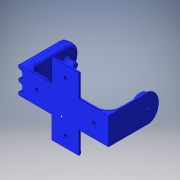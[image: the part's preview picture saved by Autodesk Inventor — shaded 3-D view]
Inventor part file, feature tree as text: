
AUTODESK INVENTOR PART (.ipt)
format: ipt  version: 2016 (Build 200138000, 138)  size: 598,016 bytes
history: native  units: in
note: dims shown in document units (in); Inventor stores cm internally (conversion verified against a paired STEP export)
features: extrude x12, sketch x12, fillet x11, hole x2
ambient origin geometry x8: Origin, YZ Plane, XZ Plane, XY Plane, X Axis, Y Axis, Z Axis, Center Point
bodies: Solid1 (feature_tree)
feature tree (37):
  extrude  "Extrusion1"  Depth=0.5197in
  extrude  "Extrusion3"  Depth=0.0787in
  sketch  "Sketch5"  dims[d9=0.9449in d10=0.0in d11=0.2835in]
  extrude  "Extrusion4"  Depth=0.2835in
  extrude  "Extrusion5"  Depth=0.2598in
  fillet  "Fillet1"  Radius=0.2598in
  fillet  "Fillet4"  Radius=0.5197in
  fillet  "Fillet5"  Radius=0.3622in
  fillet  "Fillet6"  Radius=0.1437in
  fillet  "Fillet7"  Radius=0.2224in
  extrude  "Extrusion6"  Depth=0.0787in
  sketch  "Sketch9"  dims[d24=0.0787in d25=0.0in d27=0.0787in]
  extrude  "Extrusion7"  Depth=0.1969in
  fillet  "Fillet10"  Radius=0.0197in
  fillet  "Fillet11"  Radius=0.0394in
  sketch  "Sketch10"  dims[d28=0.0787in d29=0.0in d30=0.1969in d33=0.0197in d34=0.0394in]
  extrude  "Extrusion8"  Depth=0.0197in
  extrude  "Extrusion10"  Depth=0.9449in TaperAngle=0.0deg
  extrude  "Extrusion11"  Depth=0.2598in
  sketch  "Sketch17"  dims[d43=0.2598in d44=0.2598in]
  hole  "Hole2"  [1 undecoded]
  fillet  "Fillet18"  Radius=0.1772in
  extrude  "Extrusion12"  Depth=0.0197in
  extrude  "Extrusion13"  Depth=0.0276in TaperAngle=0.0deg
  fillet  "Fillet22"  Radius=0.5197in
  hole  "Hole3"  [1 undecoded]
  extrude  "Extrusion14"  Depth=0.0276in
  fillet  "Fillet24"  Radius=0.4291in
  fillet  "Fillet25"  Radius=0.5669in
  sketch  "Sketch1"  dims[d0=1.6535in d1=0.5197in]
  sketch  "Sketch4"  dims[d2=0.0787in d3=0.0in d8=0.0787in]
  sketch  "Sketch7"  dims[d12=0.2598in d13=0.2598in d14=0.2598in d15=0.5197in d16=0.3622in d17=0.1437in d19=0.2224in]
  sketch  "Sketch15"  dims[d35=0.0394in d36=0.0197in]
  sketch  "Sketch16"  dims[d37=0.0787in d38=0.9449in d39=0.0in]
  sketch  "Sketch18"  dims[d45=0.2598in d46=0.1181in d47=0.1772in d48=0.0in]
  sketch  "Sketch19"  dims[d49=0.0394in d50=0.0197in]
  sketch  "Sketch20"  dims[d51=0.1181in d52=0.1181in d53=0.0in d82=0.5197in d83=0.5669in d84=0.5669in d85=0.4291in d86=0.0in d87=0.5669in d88=0.4291in d89=0.0in d90=0.0591in d91=0.2362in d92=0.1575in d93=0.0787in d94=90.0deg d95=0.315in d96=0.8108in d98=0.1181in d99=0.5591in d100=0.5591in d101=0.5591in d103=0.4291in d104=0.0in d106=0.0591in d107=0.4291in d108=0.0in d111=0.0748in d112=0.0591in d113=0.2362in d114=0.1575in d115=0.0787in d116=90.0deg d117=0.315in d118=0.8108in d121=0.2598in d122=0.2598in d124=0.2598in d126=0.2598in d128=0.2756in d129=0.1969in d130=0.2756in d131=0.2165in d132=0.2598in d133=0.2598in d138=0.1417in d139=0.0787in d140=0.0in d141=0.0394in d142=0.0276in]
note: 2 required parameter values undecoded (feature->parameter linkage not recoverable at this tier; creation-order binding heuristic only, values carry confidence <= 0.55)
